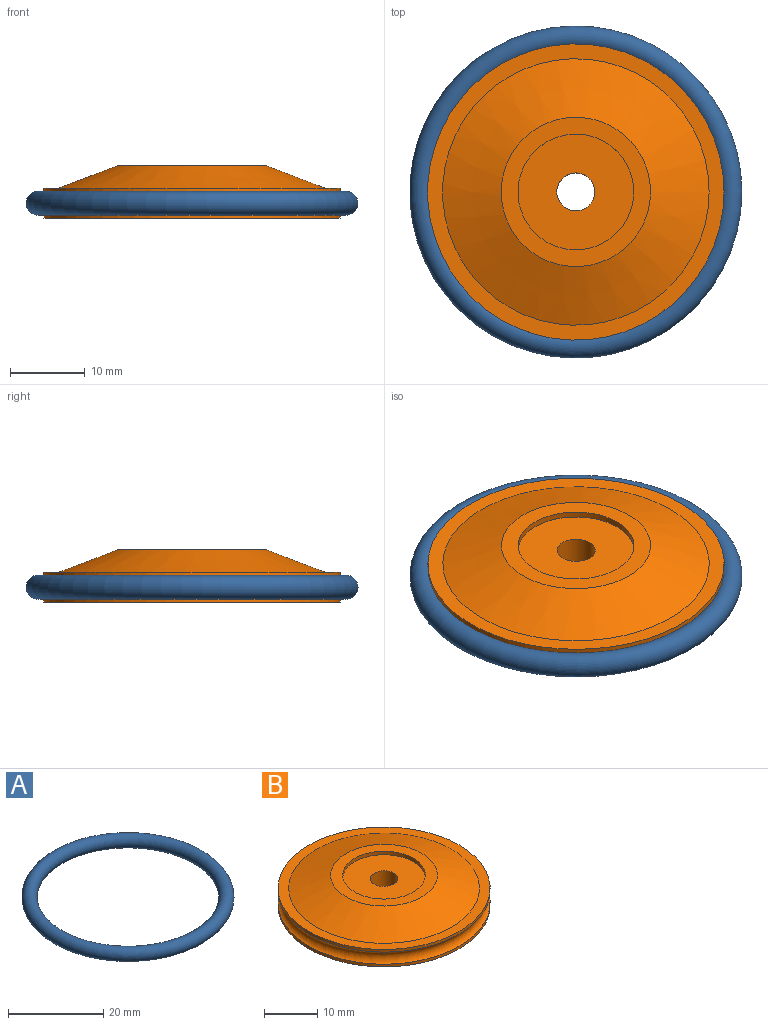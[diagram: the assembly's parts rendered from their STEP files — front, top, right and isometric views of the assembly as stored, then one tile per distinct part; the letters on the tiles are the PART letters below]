
ASSEMBLY  parts=2 mates=2
PART A: 1 faces, bbox 48.2x48.2x3.2 mm
  f0: torus R=20.65mm, axis (0,0,-1), area 1304.4mm2
PART B: 12 faces, bbox 44.7x44.7x7 mm
  f0: cylinder r=2.55mm len=5.1mm, axis (0,0,1), area 80.1mm2, adj f8,f10
  f1: torus R=20.65mm, axis (0,0,1), area 406.9mm2, adj f2,f7
  f2: cylinder r=19.85mm len=39.7mm, axis (0,0,1), area 76.6mm2, adj f1,f3
  f3: plane 39.7x39.7mm, normal (0,0,-1), area 1181.1mm2, adj f2,f11
  f4: plane 20x20mm, normal (0,0,1), area 125.5mm2, adj f5,f9
  f5: cone r=17.85mm half-angle=69.1deg, axis (0,0,-1), area 735.3mm2, adj f4,f6
  f6: plane 39.7x39.7mm, normal (0,0,1), area 236.9mm2, adj f5,f7
  f7: cylinder r=19.85mm len=39.7mm, axis (0,0,1), area 76.6mm2, adj f1,f6
  f8: plane 15.5x15.5mm, normal (0,0,1), area 168.3mm2, adj f0,f9
  f9: cylinder r=7.75mm len=15.5mm, axis (0,0,1), area 39mm2, adj f4,f8
  f10: plane 8.5x8.5mm, normal (0,0,-1), area 36.3mm2, adj f0,f11
  f11: cylinder r=4.25mm len=8.5mm, axis (0,0,-1), area 32mm2, adj f3,f10
PLACE A rot(axis=(0,0,1),179.9deg) t=(0.03,0.02,-1.34)mm
PLACE B t=(0.03,0.02,-1.34)mm fixed
MATE cylindrical A.f0 <-> B.f1  axis (0,0,-1) through (0.03,0.02,-1.34)mm
MATE planar A.f0 <-> B.f1  axis (0,0,-1) through (0.03,0.02,-1.34)mm
